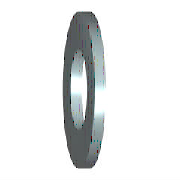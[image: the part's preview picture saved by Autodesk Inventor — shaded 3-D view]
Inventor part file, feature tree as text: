
AUTODESK INVENTOR PART (.ipt)
format: ipt  version: 2015 (Build 190159000, 159)  size: 107,008 bytes
history: native  units: mm (DEFAULTED — no unit token found)
features: extrude x1, other x1, plane x1, sketch x1
ambient origin geometry x7: Origin, YZ Plane, XY Plane, X Axis, Y Axis, Z Axis, Center Point
bodies: Solid1 (feature_tree)
feature tree (4):
  extrude  "Bryła"  Depth=5.3mm
  other  "Work Axis1"
  plane  "Work Plane1"
  sketch  "Szkic"
